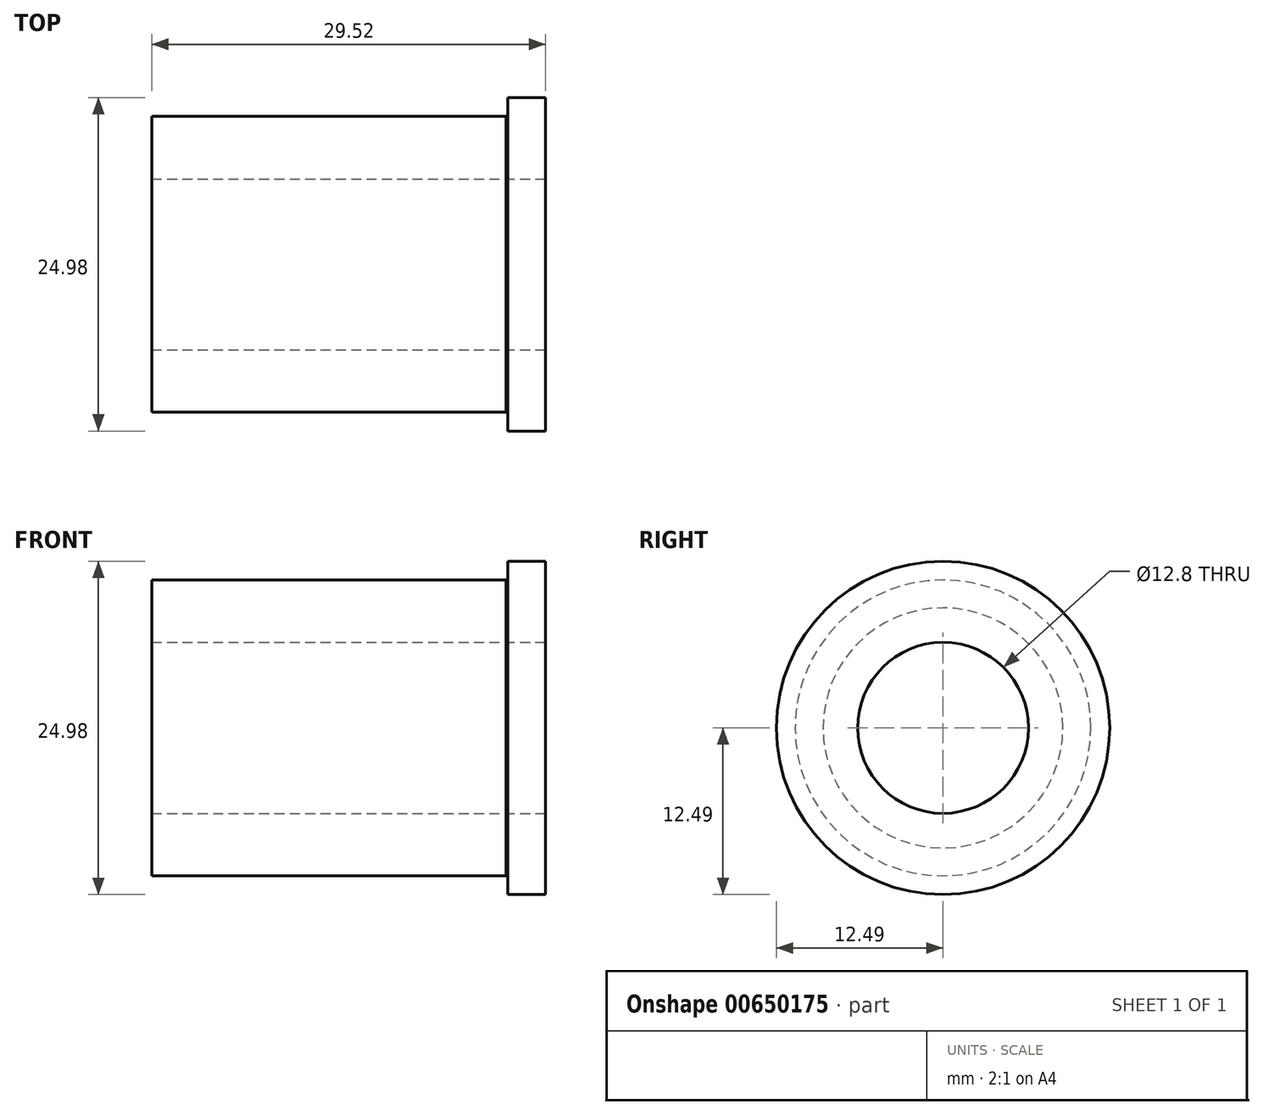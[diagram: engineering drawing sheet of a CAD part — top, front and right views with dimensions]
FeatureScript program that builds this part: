
annotation { "Feature Type Name" : "Feature", "Feature Type Description" : "" }
export const myFeature = defineFeature(function(context is Context, id is Id, definition is map)
    precondition{}
    {
        {
            var Q0;
            Q0=qCreatedBy(makeId("Right.planeOp"),FACE);
            var sketch = newSketch(context, id + "F0", { "sketchPlane" : qUnion([Q0])});
            skCircle(sketch, "E0", {"center": v(0, 0) * mm, "radius": 12.5 * mm});
            skSolve(sketch);
        }
        {
            var Q0;
            Q0=makeQuery(id+"F0.imprint","IMPRINT",FACE,{"disambiguationData":[TD([[makeQuery(id+"F0.imprint","IMPRINT",EDGE,{"derivedFrom":sQuery(id+"F0.wireOp",EDGE,"E0")}),1.0]])]});
            extrude(context, id + "F1", {"entities" : qUnion([Q0]), "depth" : 2.84 * mm, "offsetDistance" : 25.4 * mm});
        }
        {
            var Q0;
            Q0=qCreatedBy(makeId("Right.planeOp"),FACE);
            var sketch = newSketch(context, id + "F2", { "sketchPlane" : qUnion([Q0])});
            skCircle(sketch, "E1", {"center": v(0, 0) * mm, "radius": 9 * mm});
            skSolve(sketch);
        }
        {
            var Q0;
            Q0 = qSketchRegion(id + "F2", true);
            extrude(context, id + "F3", {"entities" : qUnion([Q0]), "operationType" : NewBodyOperationType.ADD, "oppositeDirection" : true, "depth" : 0.12 * mm, "offsetDistance" : 25 * mm});
        }
        {
            var Q0;
            Q0=makeQuery(id+"F3.opExtrude","CAP_FACE",FACE,{"disambiguationData":[OSD([sQuery(id+"F2.wireOp",EDGE,"E1")])],"isStart":false});
            var sketch = newSketch(context, id + "F4", { "sketchPlane" : qUnion([Q0])});
            skCircle(sketch, "E2", {"center": v(0, 0) * mm, "radius": 11.08 * mm});
            skSolve(sketch);
        }
        {
            var Q0;
            Q0 = qSketchRegion(id + "F4", true);
            extrude(context, id + "F5", {"entities" : qUnion([Q0]), "operationType" : NewBodyOperationType.ADD, "depth" : 26.56 * mm, "offsetDistance" : 25 * mm});
        }
        {
            var Q0;
            Q0=makeQuery(id+"F1.opExtrude","CAP_FACE",FACE,{"disambiguationData":[OSD([sQuery(id+"F0.wireOp",EDGE,"E0")])],"isStart":false});
            var sketch = newSketch(context, id + "F6", { "sketchPlane" : qUnion([Q0])});
            skCircle(sketch, "E3", {"center": v(0, 0) * mm, "radius": 6.4 * mm});
            skSolve(sketch);
        }
        {
            var Q0;
            Q0=makeQuery(id+"F6.imprint","IMPRINT",FACE,{"disambiguationData":[TD([[makeQuery(id+"F6.imprint","IMPRINT",EDGE,{"derivedFrom":sQuery(id+"F6.wireOp",EDGE,"E3")}),1.0]])]});
            extrude(context, id + "F7", {"entities" : qUnion([Q0]), "operationType" : NewBodyOperationType.REMOVE, "oppositeDirection" : true, "depth" : 29.56 * mm, "offsetDistance" : 25 * mm});
        }
    });
